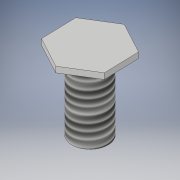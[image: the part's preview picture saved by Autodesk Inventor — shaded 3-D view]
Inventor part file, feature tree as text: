
AUTODESK INVENTOR PART (.ipt)
format: ipt  version: 2017 (Build 210142000, 142)  size: 111,104 bytes
history: native  units: in
note: dims shown in document units (in); Inventor stores cm internally (conversion verified against a paired STEP export)
features: extrude x2, thread x2, sketch x2
ambient origin geometry x8: Origin, YZ Plane, XZ Plane, XY Plane, X Axis, Y Axis, Z Axis, Center Point
bodies: Solid1 (feature_tree)
feature tree (6):
  extrude  "Extrusion1"  Depth=0.25in
  thread  "Thread1"  [1 undecoded]
  extrude  "Extrusion3"  Depth=0.02in TaperAngle=0.0deg
  thread  "Thread3"  [1 undecoded]
  sketch  "Sketch1"  dims[d0=0.5in d1=0.125in d2=0.25in d3=0.0in]
  sketch  "Sketch3"  dims[d7=1.0in d8=0.0in d11=0.02in d12=0.0in d13=1.0in d14=0.0in]
note: 2 required parameter values undecoded (feature->parameter linkage not recoverable at this tier; creation-order binding heuristic only, values carry confidence <= 0.55)
